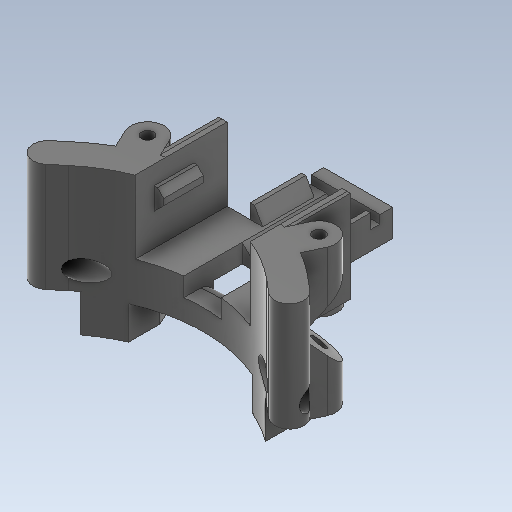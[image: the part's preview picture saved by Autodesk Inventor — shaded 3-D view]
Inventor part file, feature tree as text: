
AUTODESK INVENTOR PART (.ipt)
format: ipt  version: 2020 (Build 240168000, 168)  size: 985,088 bytes
history: native  units: mm
features: projected_geometry x35, extrude x22, sketch x21, other x6, chamfer x3, sweep x1, fillet x1
ambient origin geometry x8: Origin, YZ Plane, XZ Plane, XY Plane, X Axis, Y Axis, Z Axis, Center Point
bodies: Body1 (feature_tree)
feature tree (89):
  other  "Твердое тело1"
  extrude  "Выдавливание1"  Depth=35.0mm TaperAngle=0.0deg
  sketch  "Эскиз2"
  extrude  "Выдавливание2"  Depth=4.0mm
  sweep  "Сдвиг1"
  extrude  "Выдавливание5"  Depth=8.0mm
  extrude  "Выдавливание6"  Depth=35.0mm TaperAngle=0.0deg
  extrude  "Выдавливание7"  Depth=8.5mm
  extrude  "Выдавливание8"  TaperAngle=45.0deg  [1 undecoded]
  other  "РабПлоскость1"
  extrude  "Выдавливание9"  Depth=8.5mm
  extrude  "Выдавливание10"  TaperAngle=45.0deg  [1 undecoded]
  extrude  "Выдавливание11"  TaperAngle=0.0deg  [1 undecoded]
  sketch  "Эскиз13"
  other  "РабПлоскость2"
  sketch  "Эскиз14"
  extrude  "Выдавливание12"  Depth=5.0mm TaperAngle=0.0deg
  extrude  "Выдавливание13"  Depth=15.0mm TaperAngle=0.0deg
  other  "РабПлоскость3"
  extrude  "Выдавливание14"  Depth=15.0mm TaperAngle=0.0deg
  extrude  "Выдавливание15"  Depth=26.0mm
  extrude  "Выдавливание16"  Depth=6.0mm
  extrude  "Выдавливание17"  Depth=15.0mm TaperAngle=0.0deg
  chamfer  "Фаска1"  Distance=2.0mm
  other  "РабПлоскость4"
  sketch  "Эскиз18"
  extrude  "Выдавливание18"  Depth=1.5mm
  extrude  "Выдавливание19"  Depth=3.0mm
  extrude  "Выдавливание20"  Depth=6.0mm
  chamfer  "Фаска2"  Distance=2.5mm
  fillet  "Сопряжение1"  [1 undecoded]
  extrude  "Выдавливание21"  Depth=15.0mm TaperAngle=0.0deg
  extrude  "Выдавливание22"  Depth=7.0mm TaperAngle=0.0deg
  extrude  "Выдавливание23"  Depth=7.0mm TaperAngle=0.0deg
  other  "РабПлоскость5"
  extrude  "Выдавливание24"  Depth=40.0mm
  chamfer  "Фаска3"  Distance=2.9mm
  sketch  "Эскиз1"
  sketch  "Эскиз3"
  projected_geometry  "Спроецированная петля1"
  projected_geometry  "Спроецированная петля2"
  sketch  "3D эскиз1"
  sketch  "Эскиз4"
  sketch  "Эскиз6"
  projected_geometry  "Спроецированная петля4"
  sketch  "Эскиз7"
  projected_geometry  "Спроецированная петля5"
  sketch  "Эскиз9"
  projected_geometry  "Спроецированная петля7"
  sketch  "Эскиз11"
  projected_geometry  "Спроецированная петля8"
  sketch  "Эскиз12"
  projected_geometry  "Спроецированная петля9"
  projected_geometry  "Спроецированная петля10"
  sketch  "Эскиз15"
  sketch  "Эскиз16"
  projected_geometry  "Спроецированная петля11"
  projected_geometry  "Спроецированная петля12"
  sketch  "Эскиз17"
  projected_geometry  "Спроецированная петля13"
  projected_geometry  "Спроецированная петля14"
  projected_geometry  "Спроецированная петля15"
  projected_geometry  "Спроецированная петля16"
  sketch  "Эскиз19"
  projected_geometry  "Спроецированная петля17"
  sketch  "Эскиз20"
  projected_geometry  "Спроецированная петля18"
  projected_geometry  "Спроецированная петля19"
  projected_geometry  "Спроецированная петля20"
  projected_geometry  "Спроецированная петля21"
  projected_geometry  "Спроецированная петля22"
  projected_geometry  "Спроецированная петля23"
  sketch  "Эскиз21"
  projected_geometry  "Спроецированная петля24"
  projected_geometry  "Спроецированная петля25"
  projected_geometry  "Спроецированная петля26"
  projected_geometry  "Спроецированная петля27"
  projected_geometry  "Спроецированная петля28"
  projected_geometry  "Спроецированная петля29"
  projected_geometry  "Спроецированная петля30"
  projected_geometry  "Спроецированная петля31"
  sketch  "Эскиз22"
  projected_geometry  "Спроецированная петля32"
  projected_geometry  "Спроецированная петля33"
  sketch  "Эскиз23"
  projected_geometry  "Спроецированная петля34"
  projected_geometry  "Спроецированная петля35"
  projected_geometry  "Спроецированная петля36"
  projected_geometry  "Спроецированная петля37"
note: 4 required parameter values undecoded (feature->parameter linkage not recoverable at this tier; creation-order binding heuristic only, values carry confidence <= 0.55)
